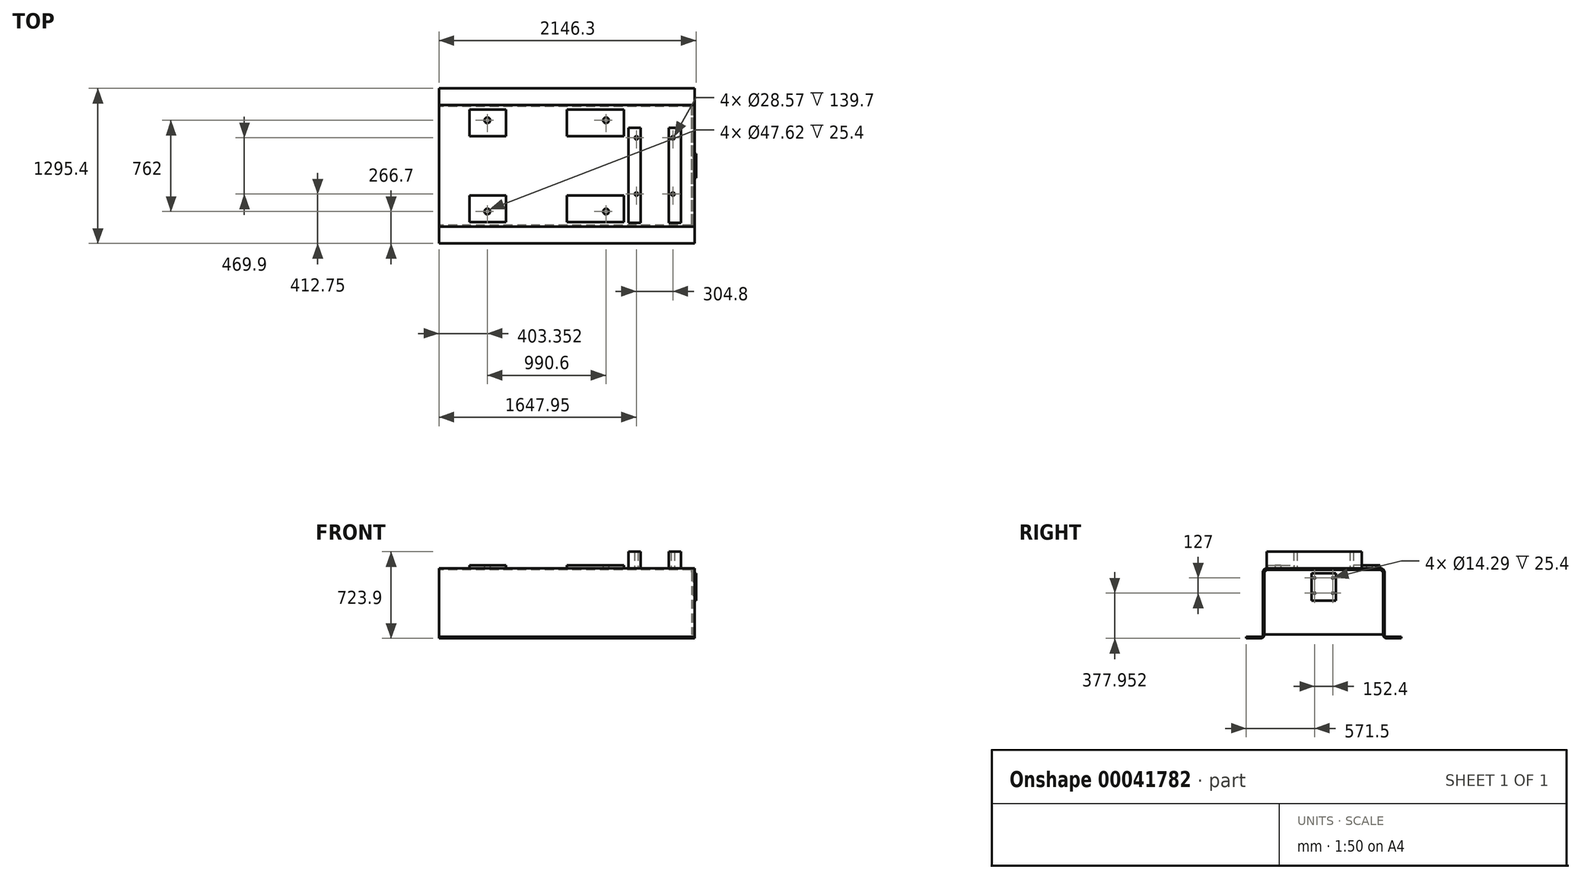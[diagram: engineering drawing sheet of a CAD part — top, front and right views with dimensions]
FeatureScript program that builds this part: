
annotation { "Feature Type Name" : "Feature", "Feature Type Description" : "" }
export const myFeature = defineFeature(function(context is Context, id is Id, definition is map)
    precondition{}
    {
        {
            var Q0;
            Q0=qCreatedBy(makeId("Right.planeOp"),FACE);
            var sketch = newSketch(context, id + "F0", { "sketchPlane" : qUnion([Q0])});
            skLineSegment(sketch, "E0.rect.bottom", {"start": v(-476.25, 292.1) * mm, "end": v(476.25, 292.1) * mm});
            skLineSegment(sketch, "E0.rect.top", {"start": v(-647.7, -292.1) * mm, "end": v(-527.05, -292.1) * mm});
            skLineSegment(sketch, "E0.rect.left", {"start": v(-508, 260.35) * mm, "end": v(-508, -260.35) * mm});
            skLineSegment(sketch, "E0.rect.right", {"start": v(508, 260.35) * mm, "end": v(508, -260.35) * mm});
            skPoint(sketch, "E0.rect.middle", {"position": v(0, 0) * mm});
            skPoint(sketch, "E1.visualSharp", {"position": v(-508, 292.1) * mm});
            skArc(sketch, "E1.filletArc", {"start": v(-476.25, 292.1) * mm, "mid": v(-498.7, 282.8) * mm, "end": v(-508, 260.35) * mm});
            skPoint(sketch, "E2.visualSharp", {"position": v(508, 292.1) * mm});
            skArc(sketch, "E2.filletArc", {"start": v(508, 260.35) * mm, "mid": v(498.7, 282.8) * mm, "end": v(476.25, 292.1) * mm});
            skLineSegment(sketch, "E3.0", {"start": v(-647.7, -279.4) * mm, "end": v(-647.7, -292.1) * mm});
            skLineSegment(sketch, "E4", {"start": v(0, 371.4) * mm, "end": v(0, -436.62) * mm, "construction": true});
            skLineSegment(sketch, "E5.0", {"start": v(-647.7, -279.4) * mm, "end": v(-527.05, -279.4) * mm});
            skPoint(sketch, "E6.newPointA", {"position": v(-508, -292.1) * mm});
            skArc(sketch, "E6.filletArc", {"start": v(-527.05, -279.4) * mm, "mid": v(-513.58, -273.82) * mm, "end": v(-508, -260.35) * mm});
            skLineSegment(sketch, "E7.0", {"start": v(-495.3, 260.35) * mm, "end": v(-495.3, -260.35) * mm});
            skArc(sketch, "E8.0", {"start": v(-527.05, -292.1) * mm, "mid": v(-504.6, -282.8) * mm, "end": v(-495.3, -260.35) * mm});
            skArc(sketch, "E9.0", {"start": v(-476.25, 279.4) * mm, "mid": v(-489.72, 273.82) * mm, "end": v(-495.3, 260.35) * mm});
            skLineSegment(sketch, "E10.0", {"start": v(-476.25, 279.4) * mm, "end": v(476.25, 279.4) * mm});
            skArc(sketch, "E11.0", {"start": v(495.3, 260.35) * mm, "mid": v(489.72, 273.82) * mm, "end": v(476.25, 279.4) * mm});
            skLineSegment(sketch, "E12.0", {"start": v(495.3, 260.35) * mm, "end": v(495.3, -260.35) * mm});
            skArc(sketch, "E13.MirrorCS", {"start": v(527.05, -279.4) * mm, "mid": v(513.58, -273.82) * mm, "end": v(508, -260.35) * mm});
            skLineSegment(sketch, "E14.MirrorCS", {"start": v(647.7, -279.4) * mm, "end": v(647.7, -292.1) * mm});
            skArc(sketch, "E15.MirrorCS", {"start": v(527.05, -292.1) * mm, "mid": v(504.6, -282.8) * mm, "end": v(495.3, -260.35) * mm});
            skLineSegment(sketch, "E16.MirrorCS", {"start": v(647.7, -292.1) * mm, "end": v(527.05, -292.1) * mm});
            skPoint(sketch, "E17.MirrorP", {"position": v(508, -292.1) * mm});
            skLineSegment(sketch, "E18.MirrorCS", {"start": v(647.7, -279.4) * mm, "end": v(527.05, -279.4) * mm});
            skSolve(sketch);
        }
        {
            var Q0;
            Q0 = qSketchRegion(id + "F0", true);
            extrude(context, id + "F1", {"entities" : qUnion([Q0]), "endBound" : BoundingType.SYMMETRIC, "depth" : 2133.6 * mm});
        }
        {
            var Q0;
            Q0=makeQuery(id+"F1.opExtrude","SWEPT_FACE",FACE,{"disambiguationData":[OSD([sQuery(id+"F0.wireOp",EDGE,"E0.rect.bottom")])]});
            var sketch = newSketch(context, id + "F2", { "sketchPlane" : qUnion([Q0])});
            skLineSegment(sketch, "E19.0", {"start": v(1066.8, -476.25) * mm, "end": v(1066.8, 476.25) * mm, "construction": true});
            skLineSegment(sketch, "E20.0", {"start": v(733.55, -476.25) * mm, "end": v(733.55, 476.25) * mm, "construction": true});
            skLineSegment(sketch, "E21.0", {"start": v(-168.15, -476.25) * mm, "end": v(-168.15, 476.25) * mm, "construction": true});
            skLineSegment(sketch, "E22", {"start": v(-1066.8, 0) * mm, "end": v(1066.8, 0) * mm, "construction": true});
            skLineSegment(sketch, "E23.0", {"start": v(-1066.8, 317.5) * mm, "end": v(1066.8, 317.5) * mm, "construction": true});
            skLineSegment(sketch, "E24.0", {"start": v(-1066.8, -469.9) * mm, "end": v(1066.8, -469.9) * mm, "construction": true});
            skLineSegment(sketch, "E25.0", {"start": v(850.9, -476.25) * mm, "end": v(850.9, 476.25) * mm, "construction": true});
            skLineSegment(sketch, "E26.0", {"start": v(952.5, -476.25) * mm, "end": v(952.5, 476.25) * mm, "construction": true});
            skLineSegment(sketch, "E27.bottom", {"start": v(952.5, 317.5) * mm, "end": v(850.9, 317.5) * mm});
            skLineSegment(sketch, "E27.top", {"start": v(952.5, -476.25) * mm, "end": v(850.9, -476.25) * mm});
            skLineSegment(sketch, "E27.left", {"start": v(952.5, 317.5) * mm, "end": v(952.5, -476.25) * mm});
            skLineSegment(sketch, "E27.right", {"start": v(850.9, 317.5) * mm, "end": v(850.9, -476.25) * mm});
            skLineSegment(sketch, "E28.0", {"start": v(885.95, -476.25) * mm, "end": v(885.95, 476.25) * mm, "construction": true});
            skLineSegment(sketch, "E29.0", {"start": v(-1066.8, 234.95) * mm, "end": v(1066.8, 234.95) * mm, "construction": true});
            skCircle(sketch, "E30", {"center": v(885.95, 234.95) * mm, "radius": 14.29 * mm});
            skCircle(sketch, "E31.MirrorC", {"center": v(885.95, -234.95) * mm, "radius": 14.29 * mm});
            skCircle(sketch, "E32.MirrorC", {"center": v(581.15, -234.95) * mm, "radius": 14.29 * mm});
            skCircle(sketch, "E33.MirrorC", {"center": v(581.15, 234.95) * mm, "radius": 14.29 * mm});
            skLineSegment(sketch, "E34.MirrorCS", {"start": v(514.6, 317.5) * mm, "end": v(616.2, 317.5) * mm});
            skLineSegment(sketch, "E35.MirrorCS", {"start": v(616.2, 317.5) * mm, "end": v(616.2, -476.25) * mm});
            skLineSegment(sketch, "E36.MirrorCS", {"start": v(514.6, 317.5) * mm, "end": v(514.6, -476.25) * mm});
            skLineSegment(sketch, "E37.MirrorCS", {"start": v(514.6, -476.25) * mm, "end": v(616.2, -476.25) * mm});
            skSolve(sketch);
        }
        {
            var Q0;
            Q0 = qSketchRegion(id + "F2", true);
            extrude(context, id + "F3", {"entities" : qUnion([Q0]), "operationType" : NewBodyOperationType.ADD, "depth" : 139.7 * mm});
        }
        {
            var Q0;
            Q0=makeQuery(id+"F2.imprint","IMPRINT",FACE,{"disambiguationData":[TD([[makeQuery(id+"F2.imprint","IMPRINT",EDGE,{"derivedFrom":sQuery(id+"F2.wireOp",EDGE,"E27.bottom")}),-1.0]])]});
            var sketch = newSketch(context, id + "F4", { "sketchPlane" : qUnion([Q0])});
            skLineSegment(sketch, "E38.0", {"start": v(-1066.8, -247.65) * mm, "end": v(1066.8, -247.65) * mm, "construction": true});
            skLineSegment(sketch, "E39.0", {"start": v(-1066.8, -469.9) * mm, "end": v(1066.8, -469.9) * mm, "construction": true});
            skLineSegment(sketch, "E40.0", {"start": v(0, -476.25) * mm, "end": v(0, 476.25) * mm, "construction": true});
            skLineSegment(sketch, "E41.0", {"start": v(476.25, -476.25) * mm, "end": v(476.25, 476.25) * mm, "construction": true});
            skLineSegment(sketch, "E42.0", {"start": v(-508, -476.25) * mm, "end": v(-508, 476.25) * mm, "construction": true});
            skLineSegment(sketch, "E43.0", {"start": v(-812.8, -476.25) * mm, "end": v(-812.8, 476.25) * mm, "construction": true});
            skLineSegment(sketch, "E44.bottom", {"start": v(-508, -469.9) * mm, "end": v(-812.8, -469.9) * mm});
            skLineSegment(sketch, "E44.top", {"start": v(-508, -247.65) * mm, "end": v(-812.8, -247.65) * mm});
            skLineSegment(sketch, "E44.left", {"start": v(-508, -469.9) * mm, "end": v(-508, -247.65) * mm});
            skLineSegment(sketch, "E44.right", {"start": v(-812.8, -469.9) * mm, "end": v(-812.8, -247.65) * mm});
            skLineSegment(sketch, "E45.bottom", {"start": v(476.25, -469.9) * mm, "end": v(0, -469.9) * mm});
            skLineSegment(sketch, "E45.top", {"start": v(476.25, -247.65) * mm, "end": v(0, -247.65) * mm});
            skLineSegment(sketch, "E45.left", {"start": v(476.25, -469.9) * mm, "end": v(476.25, -247.65) * mm});
            skLineSegment(sketch, "E45.right", {"start": v(0, -469.9) * mm, "end": v(0, -247.65) * mm});
            skLineSegment(sketch, "E46.0", {"start": v(-1066.8, -381) * mm, "end": v(1066.8, -381) * mm, "construction": true});
            skLineSegment(sketch, "E47.0", {"start": v(-663.45, -476.25) * mm, "end": v(-663.45, 476.25) * mm, "construction": true});
            skLineSegment(sketch, "E48.0", {"start": v(327.15, -476.25) * mm, "end": v(327.15, 476.25) * mm, "construction": true});
            skCircle(sketch, "E49", {"center": v(-663.45, -381) * mm, "radius": 23.81 * mm});
            skCircle(sketch, "E50", {"center": v(327.15, -381) * mm, "radius": 23.81 * mm});
            skCircle(sketch, "E51.MirrorC", {"center": v(-663.45, 381) * mm, "radius": 23.81 * mm});
            skLineSegment(sketch, "E52.MirrorCS", {"start": v(476.25, 469.9) * mm, "end": v(0, 469.9) * mm});
            skLineSegment(sketch, "E53.MirrorCS", {"start": v(-812.8, 469.9) * mm, "end": v(-812.8, 247.65) * mm});
            skLineSegment(sketch, "E54.MirrorCS", {"start": v(476.25, 469.9) * mm, "end": v(476.25, 247.65) * mm});
            skLineSegment(sketch, "E55.MirrorCS", {"start": v(-508, 469.9) * mm, "end": v(-508, 247.65) * mm});
            skLineSegment(sketch, "E56.MirrorCS", {"start": v(-508, 469.9) * mm, "end": v(-812.8, 469.9) * mm});
            skCircle(sketch, "E57.MirrorC", {"center": v(327.15, 381) * mm, "radius": 23.81 * mm});
            skLineSegment(sketch, "E58.MirrorCS", {"start": v(476.25, 247.65) * mm, "end": v(0, 247.65) * mm});
            skLineSegment(sketch, "E59.MirrorCS", {"start": v(-508, 247.65) * mm, "end": v(-812.8, 247.65) * mm});
            skLineSegment(sketch, "E60.MirrorCS", {"start": v(0, 469.9) * mm, "end": v(0, 247.65) * mm});
            skSolve(sketch);
        }
        {
            var Q0;
            Q0 = qSketchRegion(id + "F4", true);
            extrude(context, id + "F5", {"entities" : qUnion([Q0]), "operationType" : NewBodyOperationType.ADD, "depth" : 25.4 * mm});
        }
        {
            var Q0;
            Q0=makeQuery(id+"F1.opExtrude","CAP_FACE",FACE,{"disambiguationData":[OSD([sQuery(id+"F0.wireOp",EDGE,"E0.rect.bottom"),sQuery(id+"F0.wireOp",EDGE,"E0.rect.top"),sQuery(id+"F0.wireOp",EDGE,"E0.rect.left"),sQuery(id+"F0.wireOp",EDGE,"E0.rect.right"),sQuery(id+"F0.wireOp",EDGE,"E1.filletArc"),sQuery(id+"F0.wireOp",EDGE,"E2.filletArc"),sQuery(id+"F0.wireOp",EDGE,"E3.0"),sQuery(id+"F0.wireOp",EDGE,"E5.0"),sQuery(id+"F0.wireOp",EDGE,"E6.filletArc"),sQuery(id+"F0.wireOp",EDGE,"E7.0"),sQuery(id+"F0.wireOp",EDGE,"E8.0"),sQuery(id+"F0.wireOp",EDGE,"E9.0"),sQuery(id+"F0.wireOp",EDGE,"E10.0"),sQuery(id+"F0.wireOp",EDGE,"E12.0"),sQuery(id+"F0.wireOp",EDGE,"E11.0"),sQuery(id+"F0.wireOp",EDGE,"E13.MirrorCS"),sQuery(id+"F0.wireOp",EDGE,"E14.MirrorCS"),sQuery(id+"F0.wireOp",EDGE,"E15.MirrorCS"),sQuery(id+"F0.wireOp",EDGE,"E16.MirrorCS"),sQuery(id+"F0.wireOp",EDGE,"E18.MirrorCS")])],"isStart":false});
            cPlane(context, id + "F6", {"entities" : qUnion([Q0]), "cplaneType" : CPlaneType.OFFSET, "offset" : 25.4 * mm, "oppositeDirection" : true, "width" : 152.4 * mm, "height" : 152.4 * mm});
        }
        {
            var Q0;
            Q0=qCreatedBy(id+"F6.planeOp",FACE);
            var sketch = newSketch(context, id + "F7", { "sketchPlane" : qUnion([Q0])});
            skLineSegment(sketch, "E61.0", {"start": v(495.3, 260.35) * mm, "end": v(495.3, -260.35) * mm});
            skLineSegment(sketch, "E62.0", {"start": v(-476.25, 279.4) * mm, "end": v(476.25, 279.4) * mm});
            skLineSegment(sketch, "E63.0", {"start": v(-495.3, 260.35) * mm, "end": v(-495.3, -260.35) * mm});
            skLineSegment(sketch, "E64", {"start": v(-495.3, 260.35) * mm, "end": v(-476.25, 279.4) * mm});
            skLineSegment(sketch, "E65", {"start": v(476.25, 279.4) * mm, "end": v(495.3, 260.35) * mm});
            skLineSegment(sketch, "E66", {"start": v(-495.3, -260.35) * mm, "end": v(495.3, -260.35) * mm});
            skSolve(sketch);
        }
        {
            var Q0;
            Q0 = qSketchRegion(id + "F7", true);
            extrude(context, id + "F8", {"entities" : qUnion([Q0]), "operationType" : NewBodyOperationType.ADD, "depth" : 12.7 * mm});
        }
        {
            var Q0;
            Q0=makeQuery(id+"F8.opExtrude","CAP_FACE",FACE,{"disambiguationData":[OSD([sQuery(id+"F7.wireOp",EDGE,"E61.0"),sQuery(id+"F7.wireOp",EDGE,"E62.0"),sQuery(id+"F7.wireOp",EDGE,"E63.0"),sQuery(id+"F7.wireOp",EDGE,"E64"),sQuery(id+"F7.wireOp",EDGE,"E65"),sQuery(id+"F7.wireOp",EDGE,"E66")])],"isStart":false});
            var sketch = newSketch(context, id + "F9", { "sketchPlane" : qUnion([Q0])});
            skLineSegment(sketch, "E67.0", {"start": v(317.5, 431.8) * mm, "end": v(-476.25, 431.8) * mm, "construction": true});
            skLineSegment(sketch, "E68.0", {"start": v(317.5, 212.85) * mm, "end": v(-476.25, 212.85) * mm, "construction": true});
            skLineSegment(sketch, "E69.0", {"start": v(317.5, 85.85) * mm, "end": v(-476.25, 85.85) * mm, "construction": true});
            skLineSegment(sketch, "E70.0", {"start": v(647.7, 250.83) * mm, "end": v(0, 250.83) * mm, "construction": true});
            skLineSegment(sketch, "E71", {"start": v(0, 0) * mm, "end": v(0, 378.53) * mm, "construction": true});
            skLineSegment(sketch, "E72.0", {"start": v(647.7, 22.23) * mm, "end": v(0, 22.23) * mm, "construction": true});
            skLineSegment(sketch, "E73.0", {"start": v(101.6, 0) * mm, "end": v(101.6, 378.53) * mm, "construction": true});
            skLineSegment(sketch, "E74.0", {"start": v(76.2, 0) * mm, "end": v(76.2, 378.53) * mm, "construction": true});
            skLineSegment(sketch, "E75.bottom", {"start": v(101.6, 250.83) * mm, "end": v(0, 250.83) * mm});
            skLineSegment(sketch, "E75.top", {"start": v(101.6, 22.23) * mm, "end": v(0, 22.23) * mm});
            skLineSegment(sketch, "E75.left", {"start": v(101.6, 250.83) * mm, "end": v(101.6, 22.23) * mm});
            skLineSegment(sketch, "E75.right", {"start": v(0, 250.83) * mm, "end": v(0, 22.23) * mm});
            skCircle(sketch, "E76", {"center": v(76.2, 212.85) * mm, "radius": 7.14 * mm});
            skCircle(sketch, "E77", {"center": v(76.2, 85.85) * mm, "radius": 7.14 * mm});
            skCircle(sketch, "E78.MirrorC", {"center": v(-76.2, 85.85) * mm, "radius": 7.14 * mm});
            skCircle(sketch, "E79.MirrorC", {"center": v(-76.2, 212.85) * mm, "radius": 7.14 * mm});
            skLineSegment(sketch, "E80.MirrorCS", {"start": v(-101.6, 250.83) * mm, "end": v(0, 250.83) * mm});
            skLineSegment(sketch, "E81.MirrorCS", {"start": v(-101.6, 22.23) * mm, "end": v(0, 22.23) * mm});
            skLineSegment(sketch, "E82.MirrorCS", {"start": v(-101.6, 250.83) * mm, "end": v(-101.6, 22.23) * mm});
            skSolve(sketch);
        }
        {
            var Q0;
            Q0 = qSketchRegion(id + "F9", true);
            extrude(context, id + "F10", {"entities" : qUnion([Q0]), "operationType" : NewBodyOperationType.ADD, "depth" : 25.4 * mm});
        }
    });
